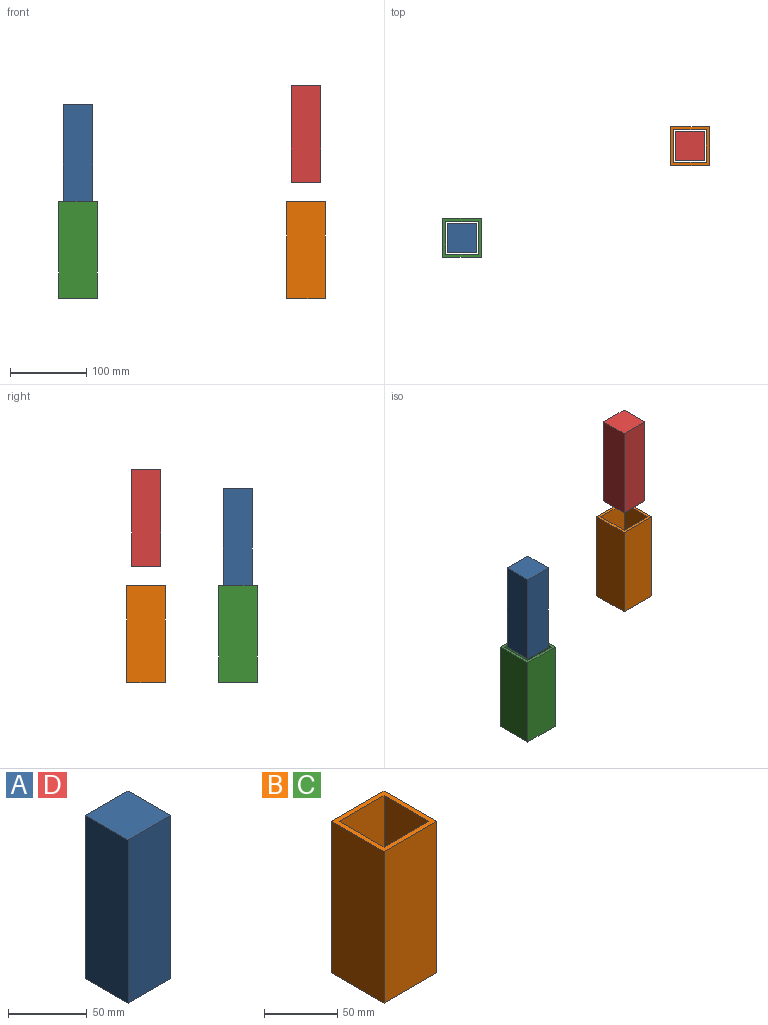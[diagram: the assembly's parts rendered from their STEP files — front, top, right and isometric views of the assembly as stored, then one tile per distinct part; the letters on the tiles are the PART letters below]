
ASSEMBLY  parts=4 mates=2
PART A: 6 faces, bbox 38.1x38.1x127 mm
  f0: plane 127x38.1mm, normal (1,0,0), area 4838.7mm2, adj f1,f3,f4,f5
  f1: plane 127x38.1mm, normal (0,1,0), area 4838.7mm2, adj f0,f2,f4,f5
  f2: plane 127x38.1mm, normal (-1,0,0), area 4838.7mm2, adj f1,f3,f4,f5
  f3: plane 127x38.1mm, normal (0,-1,0), area 4838.7mm2, adj f0,f2,f4,f5
  f4: plane 38.1x38.1mm, normal (0,0,1), area 1451.6mm2, adj f0,f1,f2,f3
  f5: plane 38.1x38.1mm, normal (0,0,-1), area 1451.6mm2, adj f0,f1,f2,f3
PART B: 10 faces, bbox 50.8x50.8x127 mm
  f0: plane 127x43.18mm, normal (0,-1,0), area 5483.9mm2, adj f1,f7,f8,f9
  f1: plane 127x43.18mm, normal (-1,0,0), area 5483.9mm2, adj f0,f2,f8,f9
  f2: plane 127x43.18mm, normal (0,1,0), area 5483.9mm2, adj f1,f7,f8,f9
  f3: plane 127x50.8mm, normal (1,0,0), area 6451.6mm2, adj f4,f6,f8,f9
  f4: plane 127x50.8mm, normal (0,1,0), area 6451.6mm2, adj f3,f5,f8,f9
  f5: plane 127x50.8mm, normal (-1,0,0), area 6451.6mm2, adj f4,f6,f8,f9
  f6: plane 127x50.8mm, normal (0,-1,0), area 6451.6mm2, adj f3,f5,f8,f9
  f7: plane 127x43.18mm, normal (1,0,0), area 5483.9mm2, adj f0,f2,f8,f9
  f8: plane 50.8x50.8mm, normal (0,0,1), area 716.1mm2, adj f0,f1,f2,f3,f4,f5,f6,f7
  f9: plane 50.8x50.8mm, normal (0,0,-1), area 716.1mm2, adj f0,f1,f2,f3,f4,f5,f6,f7
PART C: same geometry as B
PART D: same geometry as A
PLACE A rot(axis=(0,0,1),0deg) t=(-9.29,126.94,322.87)mm
PLACE B rot(axis=(0.42,-0.18,-0.89),0deg) t=(289.46,247.24,195.41)mm fixed
PLACE C t=(-9.29,126.94,195.87)mm fixed
PLACE D t=(289.46,247.24,347.81)mm
MATE slider C.f8 <-> A.f5  axis (0,0,1) through (-9.29,126.94,322.87)mm
MATE slider B.f8 <-> D.f5  axis (0,0,1) through (289.46,247.24,322.41)mm
